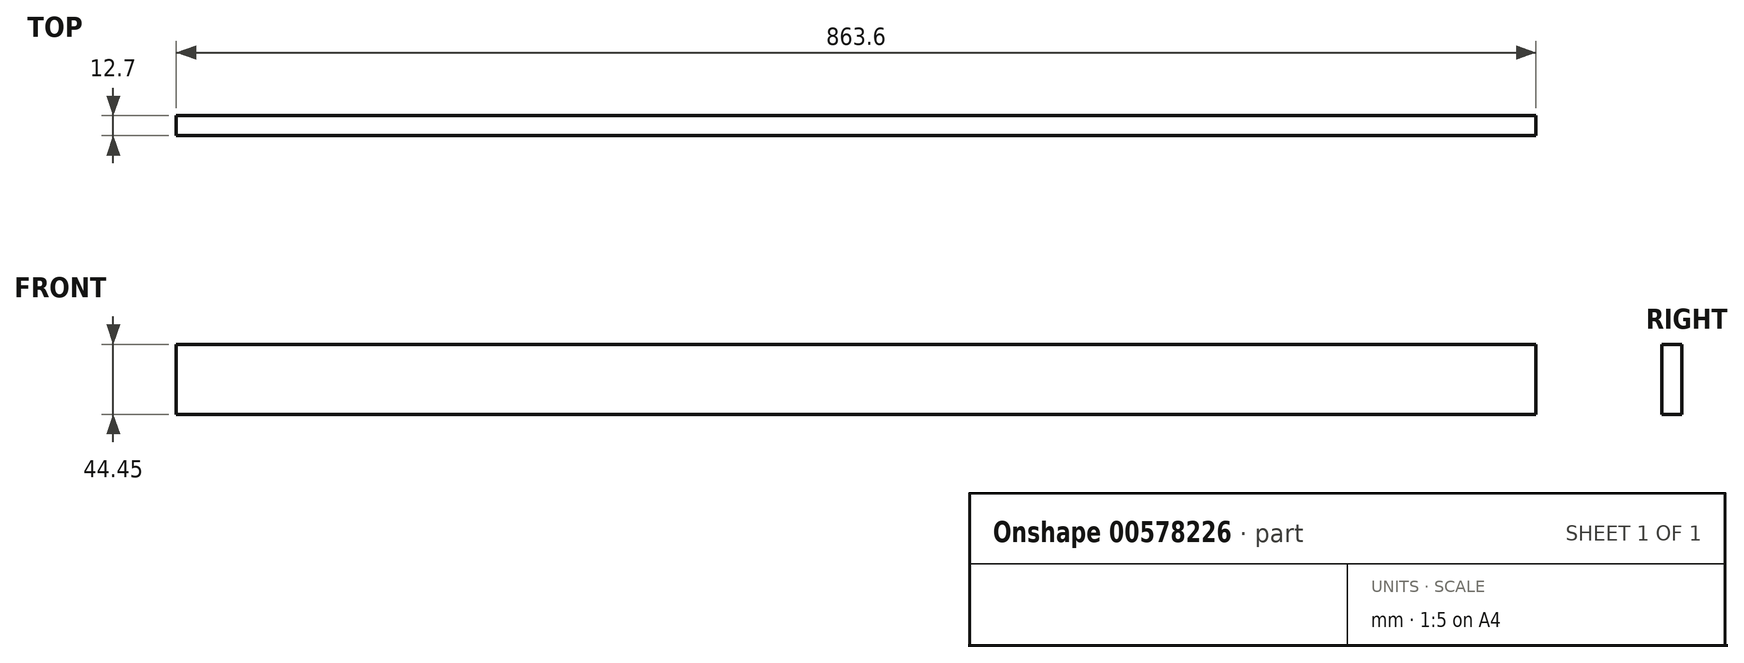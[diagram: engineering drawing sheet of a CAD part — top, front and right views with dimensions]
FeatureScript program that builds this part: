
annotation { "Feature Type Name" : "Feature", "Feature Type Description" : "" }
export const myFeature = defineFeature(function(context is Context, id is Id, definition is map)
    precondition{}
    {
        {
            var Q0;
            Q0=qCreatedBy(makeId("Front.planeOp"),FACE);
            var sketch = newSketch(context, id + "F0", { "sketchPlane" : qUnion([Q0])});
            skLineSegment(sketch, "E0.bottom", {"start": v(-451.44, -65.34) * mm, "end": v(412.16, -65.34) * mm});
            skLineSegment(sketch, "E0.top", {"start": v(-451.44, -109.8) * mm, "end": v(412.16, -109.8) * mm});
            skLineSegment(sketch, "E0.left", {"start": v(-451.44, -65.34) * mm, "end": v(-451.44, -109.8) * mm});
            skLineSegment(sketch, "E0.right", {"start": v(412.16, -65.34) * mm, "end": v(412.16, -109.8) * mm});
            skSolve(sketch);
        }
        {
            var Q0;
            Q0 = qSketchRegion(id + "F0", true);
            extrude(context, id + "F1", {"entities" : qUnion([Q0]), "depth" : 12.7 * mm, "offsetDistance" : 25.4 * mm});
        }
    });
